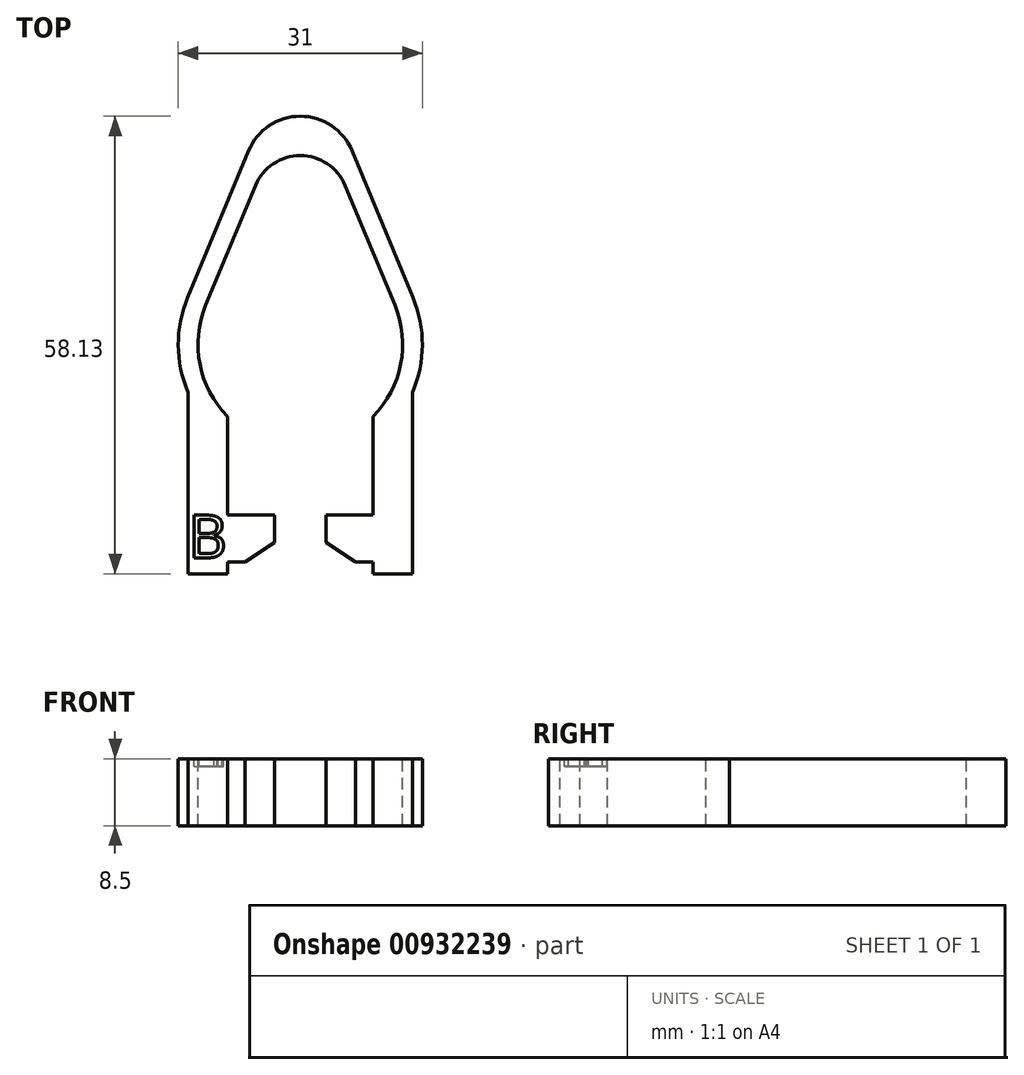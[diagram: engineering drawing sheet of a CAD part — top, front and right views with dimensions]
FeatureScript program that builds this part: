
annotation { "Feature Type Name" : "Feature", "Feature Type Description" : "" }
export const myFeature = defineFeature(function(context is Context, id is Id, definition is map)
    precondition{}
    {
        {
            var Q0;
            Q0=qCreatedBy(makeId("Top.planeOp"),FACE);
            var sketch = newSketch(context, id + "F0", { "sketchPlane" : qUnion([Q0])});
            skPoint(sketch, "E0", {"position": v(0, 0) * mm});
            skPoint(sketch, "E1", {"position": v(-13, 0) * mm});
            skPoint(sketch, "E2", {"position": v(13, 0) * mm});
            skArc(sketch, "E3", {"start": v(-12, 4.98) * mm, "mid": v(-12.76, -2.5) * mm, "end": v(-9.25, -9.13) * mm});
            skPoint(sketch, "E4", {"position": v(-9.18, 9.2) * mm});
            skPoint(sketch, "E5", {"position": v(9.18, 9.2) * mm});
            skLineSegment(sketch, "E6", {"start": v(-9.18, 9.2) * mm, "end": v(-13, 0) * mm, "construction": true});
            skLineSegment(sketch, "E7", {"start": v(9.18, 9.2) * mm, "end": v(13, 0) * mm, "construction": true});
            skLineSegment(sketch, "E8", {"start": v(-12, 4.98) * mm, "end": v(-11.1, 4.6) * mm, "construction": true});
            skLineSegment(sketch, "E9", {"start": v(11.1, 4.6) * mm, "end": v(12, 4.98) * mm, "construction": true});
            skLineSegment(sketch, "E10", {"start": v(-12, 4.98) * mm, "end": v(-5.7, 20.2) * mm});
            skLineSegment(sketch, "E11", {"start": v(12, 4.98) * mm, "end": v(5.7, 20.2) * mm});
            skLineSegment(sketch, "E12", {"start": v(-5.7, 20.2) * mm, "end": v(5.7, 20.2) * mm, "construction": true});
            skArc(sketch, "E13", {"start": v(-5.7, 20.2) * mm, "mid": v(0, 24) * mm, "end": v(5.7, 20.2) * mm});
            skPoint(sketch, "E14", {"position": v(0, 24) * mm});
            skPoint(sketch, "E15", {"position": v(0, -13) * mm});
            skArc(sketch, "E16.trimOffspring", {"start": v(9.18, 9.2) * mm, "mid": v(0, 13) * mm, "end": v(-9.18, 9.2) * mm, "construction": true});
            skPoint(sketch, "E17", {"position": v(-15.5, 0) * mm});
            skPoint(sketch, "E18", {"position": v(15.5, 0) * mm});
            skArc(sketch, "E19", {"start": v(-14.32, 5.94) * mm, "mid": v(-15.2, 3.03) * mm, "end": v(-15.5, 0) * mm});
            skPoint(sketch, "E20", {"position": v(-10.95, 10.97) * mm});
            skPoint(sketch, "E21", {"position": v(10.95, 10.97) * mm});
            skLineSegment(sketch, "E22", {"start": v(-10.95, 10.97) * mm, "end": v(-15.5, 0) * mm, "construction": true});
            skLineSegment(sketch, "E23", {"start": v(10.95, 10.97) * mm, "end": v(15.5, 0) * mm, "construction": true});
            skLineSegment(sketch, "E24", {"start": v(-14.32, 5.94) * mm, "end": v(-13.23, 5.48) * mm, "construction": true});
            skLineSegment(sketch, "E25", {"start": v(13.23, 5.48) * mm, "end": v(14.32, 5.94) * mm, "construction": true});
            skLineSegment(sketch, "E26", {"start": v(-14.32, 5.94) * mm, "end": v(-6.57, 24.6) * mm});
            skLineSegment(sketch, "E27", {"start": v(14.32, 5.94) * mm, "end": v(6.57, 24.6) * mm});
            skLineSegment(sketch, "E28", {"start": v(-6.57, 24.6) * mm, "end": v(6.57, 24.6) * mm, "construction": true});
            skArc(sketch, "E29", {"start": v(-6.57, 24.6) * mm, "mid": v(0, 29) * mm, "end": v(6.57, 24.6) * mm});
            skPoint(sketch, "E30", {"position": v(0, 29) * mm});
            skLineSegment(sketch, "E31", {"start": v(-15.5, 0) * mm, "end": v(0, 0) * mm, "construction": true});
            skPoint(sketch, "E32", {"position": v(-9.25, -12.44) * mm});
            skPoint(sketch, "E33", {"position": v(9.25, -12.44) * mm});
            skLineSegment(sketch, "E34", {"start": v(-9.25, -12.44) * mm, "end": v(9.25, -12.44) * mm, "construction": true});
            skLineSegment(sketch, "E35", {"start": v(-9.25, -12.44) * mm, "end": v(-9.25, -21.63) * mm});
            skLineSegment(sketch, "E36", {"start": v(9.25, -12.44) * mm, "end": v(9.25, -21.63) * mm});
            skPoint(sketch, "E37", {"position": v(-14.25, -6.1) * mm});
            skPoint(sketch, "E38", {"position": v(14.25, -6.1) * mm});
            skLineSegment(sketch, "E39", {"start": v(-14.25, -6.1) * mm, "end": v(14.25, -6.1) * mm, "construction": true});
            skLineSegment(sketch, "E40", {"start": v(-14.25, -6.1) * mm, "end": v(-14.25, -22.63) * mm});
            skLineSegment(sketch, "E41", {"start": v(14.25, -6.1) * mm, "end": v(14.25, -22.62) * mm});
            skLineSegment(sketch, "E42", {"start": v(0, 29) * mm, "end": v(0, -13) * mm, "construction": true});
            skLineSegment(sketch, "E43", {"start": v(-10.45, 15.27) * mm, "end": v(-8.14, 14.32) * mm, "construction": true});
            skLineSegment(sketch, "E44", {"start": v(10.45, 15.27) * mm, "end": v(8.14, 14.32) * mm, "construction": true});
            skLineSegment(sketch, "E45", {"start": v(-3.25, -22.63) * mm, "end": v(-3.25, -25.13) * mm});
            skLineSegment(sketch, "E46", {"start": v(-3.25, -25.13) * mm, "end": v(-7, -27.63) * mm});
            skLineSegment(sketch, "E47", {"start": v(-9.25, -29.13) * mm, "end": v(-14.25, -29.13) * mm});
            skLineSegment(sketch, "E48", {"start": v(-14.25, -29.13) * mm, "end": v(-14.25, -22.63) * mm});
            skLineSegment(sketch, "E49", {"start": v(3.25, -22.63) * mm, "end": v(3.25, -25.13) * mm});
            skLineSegment(sketch, "E50", {"start": v(3.25, -25.13) * mm, "end": v(7, -27.63) * mm});
            skLineSegment(sketch, "E51", {"start": v(9.25, -29.13) * mm, "end": v(14.25, -29.13) * mm});
            skLineSegment(sketch, "E52", {"start": v(14.25, -29.13) * mm, "end": v(14.25, -22.62) * mm});
            skLineSegment(sketch, "E53", {"start": v(-14.25, -12.44) * mm, "end": v(-9.25, -12.44) * mm, "construction": true});
            skLineSegment(sketch, "E54", {"start": v(9.25, -12.44) * mm, "end": v(14.25, -12.44) * mm, "construction": true});
            skLineSegment(sketch, "E55", {"start": v(-9.25, -12.44) * mm, "end": v(-9.25, -9.13) * mm});
            skLineSegment(sketch, "E56", {"start": v(9.25, -12.44) * mm, "end": v(9.25, -9.13) * mm});
            skArc(sketch, "E57.trimOffspring", {"start": v(9.25, -9.13) * mm, "mid": v(12.76, -2.5) * mm, "end": v(12, 4.98) * mm});
            skArc(sketch, "E58.trimOffspring", {"start": v(15.5, 0) * mm, "mid": v(15.2, 3.03) * mm, "end": v(14.32, 5.94) * mm});
            skArc(sketch, "E59", {"start": v(14.25, -6.1) * mm, "mid": v(15.18, -3.11) * mm, "end": v(15.5, 0) * mm});
            skArc(sketch, "E60.trimOffspring", {"start": v(-14.32, 5.94) * mm, "mid": v(-15.5, -0.09) * mm, "end": v(-14.25, -6.1) * mm});
            skPoint(sketch, "E61", {"position": v(0, 20.2) * mm});
            skArc(sketch, "E62", {"start": v(5.7, 20.2) * mm, "mid": v(0, 23.5) * mm, "end": v(-5.7, 20.2) * mm});
            skPoint(sketch, "E63", {"position": v(0, 23.5) * mm});
            skLineSegment(sketch, "E64", {"start": v(-9.25, -21.63) * mm, "end": v(-3.25, -21.63) * mm});
            skLineSegment(sketch, "E65", {"start": v(-3.25, -22.63) * mm, "end": v(-3.25, -21.63) * mm});
            skLineSegment(sketch, "E66", {"start": v(9.25, -21.63) * mm, "end": v(3.25, -21.63) * mm});
            skLineSegment(sketch, "E67", {"start": v(3.25, -21.63) * mm, "end": v(3.25, -22.63) * mm});
            skPoint(sketch, "E68.orphan", {"position": v(-9.25, -22.63) * mm});
            skPoint(sketch, "E69.orphan", {"position": v(9.25, -22.62) * mm});
            skText(sketch, "E70", { "text": "B", "fontName": "OpenSans-Regular.ttf"});
            skLineSegment(sketch, "E71", {"start": v(-9.25, -27.63) * mm, "end": v(-9.25, -29.13) * mm});
            skLineSegment(sketch, "E72", {"start": v(-9.25, -27.63) * mm, "end": v(-7, -27.63) * mm});
            skLineSegment(sketch, "E73", {"start": v(9.25, -29.13) * mm, "end": v(9.25, -27.63) * mm});
            skLineSegment(sketch, "E74", {"start": v(9.25, -27.63) * mm, "end": v(7, -27.63) * mm});
            const initialGuessF0  = {"E70": [-0.01425, -0.0271, 1, 0, 0.00547]};
            skSetInitialGuess(sketch, initialGuessF0);
            skSolve(sketch);
        }
        {
            var Q0;
            Q0=makeQuery(id+"F0.imprint","IMPRINT",FACE,{"disambiguationData":[TD([[makeQuery(id+"F0.imprint","IMPRINT",EDGE,{"derivedFrom":sQuery(id+"F0.wireOp",EDGE,"E70.sketch_text.stroke-18")}),1.0]])]});
            var Q1;
            Q1=makeQuery(id+"F0.imprint","IMPRINT",FACE,{"disambiguationData":[TD([[makeQuery(id+"F0.imprint","IMPRINT",EDGE,{"derivedFrom":sQuery(id+"F0.wireOp",EDGE,"E70.sketch_text.stroke-0")}),-1.0]])]});
            var Q2;
            Q2=makeQuery(id+"F0.imprint","IMPRINT",FACE,{"disambiguationData":[TD([[makeQuery(id+"F0.imprint","IMPRINT",EDGE,{"derivedFrom":sQuery(id+"F0.wireOp",EDGE,"E3")}),-1.0]])]});
            var Q3;
            Q3=makeQuery(id+"F0.imprint","IMPRINT",FACE,{"disambiguationData":[TD([[makeQuery(id+"F0.imprint","IMPRINT",EDGE,{"derivedFrom":sQuery(id+"F0.wireOp",EDGE,"E70.sketch_text.stroke-11")}),1.0]])]});
            extrude(context, id + "F1", {"entities" : qUnion([Q0, Q1, Q2, Q3]), "oppositeDirection" : true, "depth" : 8.5 * mm, "offsetDistance" : 25 * mm});
        }
        {
            var Q0;
            Q0=makeQuery(id+"F0.imprint","IMPRINT",FACE,{"disambiguationData":[TD([[makeQuery(id+"F0.imprint","IMPRINT",EDGE,{"derivedFrom":sQuery(id+"F0.wireOp",EDGE,"E70.sketch_text.stroke-0")}),-1.0]])]});
            extrude(context, id + "F2", {"entities" : qUnion([Q0]), "operationType" : NewBodyOperationType.REMOVE, "oppositeDirection" : true, "depth" : 1 * mm, "offsetDistance" : 25 * mm});
        }
    });
